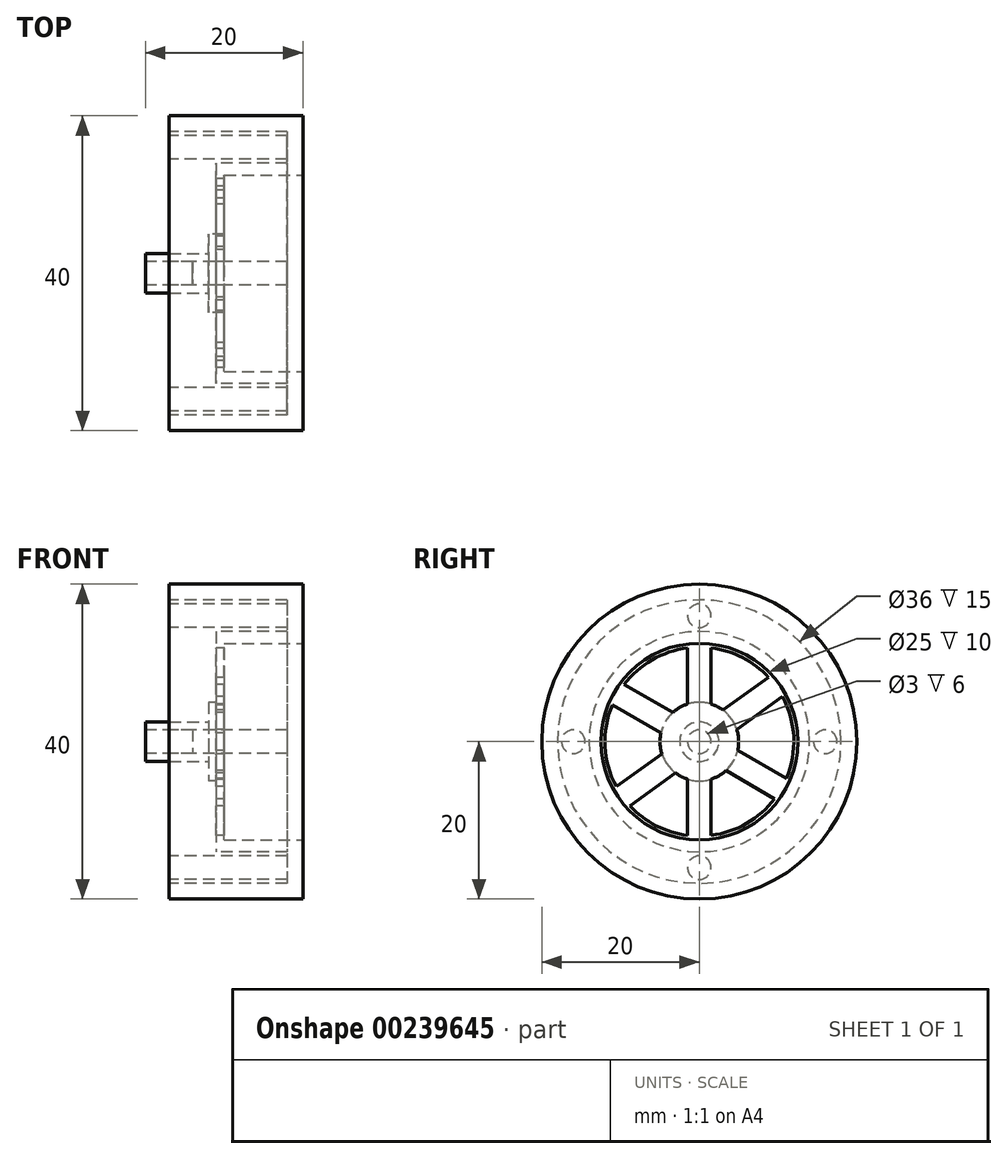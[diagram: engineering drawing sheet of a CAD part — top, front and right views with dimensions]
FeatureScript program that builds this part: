
annotation { "Feature Type Name" : "Feature", "Feature Type Description" : "" }
export const myFeature = defineFeature(function(context is Context, id is Id, definition is map)
    precondition{}
    {
        {
            var Q0;
            Q0=qCreatedBy(makeId("Right.planeOp"),FACE);
            var sketch = newSketch(context, id + "F0", { "sketchPlane" : qUnion([Q0])});
            skCircle(sketch, "E0", {"center": v(0, 0) * mm, "radius": 20 * mm});
            skSolve(sketch);
        }
        {
            var Q0;
            Q0=makeQuery(id+"F0.imprint","IMPRINT",FACE,{"disambiguationData":[TD([[makeQuery(id+"F0.imprint","IMPRINT",EDGE,{"derivedFrom":sQuery(id+"F0.wireOp",EDGE,"E0")}),1.0]])]});
            extrude(context, id + "F1", {"entities" : qUnion([Q0]), "depth" : 17 * mm});
        }
        {
            var Q0;
            Q0=makeQuery(id+"F1.opExtrude","CAP_FACE",FACE,{"disambiguationData":[OSD([sQuery(id+"F0.wireOp",EDGE,"E0")])],"isStart":true});
            var sketch = newSketch(context, id + "F2", { "sketchPlane" : qUnion([Q0])});
            skCircle(sketch, "E1", {"center": v(0, 0) * mm, "radius": 14 * mm});
            skCircle(sketch, "E2", {"center": v(0, 0) * mm, "radius": 18 * mm});
            skLineSegment(sketch, "E3", {"start": v(-17.5, 0) * mm, "end": v(-14.5, 0) * mm});
            skLineSegment(sketch, "E4", {"start": v(0, -14.5) * mm, "end": v(0, -17.5) * mm});
            skLineSegment(sketch, "E5", {"start": v(14.5, 0) * mm, "end": v(17.5, 0) * mm});
            skLineSegment(sketch, "E6", {"start": v(0, 17.5) * mm, "end": v(0, 14.5) * mm});
            skPoint(sketch, "E7", {"position": v(0, 16) * mm});
            skPoint(sketch, "E8", {"position": v(-16, 0) * mm});
            skPoint(sketch, "E9", {"position": v(0, -16) * mm});
            skPoint(sketch, "E10", {"position": v(16, 0) * mm});
            skCircle(sketch, "E11", {"center": v(0, 16) * mm, "radius": 1.5 * mm});
            skCircle(sketch, "E12", {"center": v(-16, 0) * mm, "radius": 1.5 * mm});
            skCircle(sketch, "E13", {"center": v(0, -16) * mm, "radius": 1.5 * mm});
            skCircle(sketch, "E14", {"center": v(16, 0) * mm, "radius": 1.5 * mm});
            skPoint(sketch, "E15.orphan", {"position": v(-18, 0) * mm});
            skPoint(sketch, "E16.orphan", {"position": v(-14, 0) * mm});
            skPoint(sketch, "E17.orphan", {"position": v(0, 14) * mm});
            skPoint(sketch, "E18.orphan", {"position": v(0, 18) * mm});
            skPoint(sketch, "E19.orphan", {"position": v(14, 0) * mm});
            skPoint(sketch, "E20.orphan", {"position": v(18, 0) * mm});
            skPoint(sketch, "E21.orphan", {"position": v(0, -14) * mm});
            skPoint(sketch, "E22.orphan", {"position": v(0, -18) * mm});
            skSolve(sketch);
        }
        {
            var Q0;
            Q0=makeQuery(id+"F2.imprint","IMPRINT",FACE,{"disambiguationData":[TD([[makeQuery(id+"F2.imprint","IMPRINT",EDGE,{"derivedFrom":sQuery(id+"F2.wireOp",EDGE,"E1")}),-1.0]])]});
            extrude(context, id + "F3", {"entities" : qUnion([Q0]), "operationType" : NewBodyOperationType.REMOVE, "oppositeDirection" : true, "depth" : 15 * mm});
        }
        {
            var Q0;
            Q0=makeQuery(id+"F3.boolean.opBoolean","SPLIT",FACE,{"disambiguationData":[TD([makeQuery(id+"F3.opExtrude","SWEPT_FACE",FACE,{"disambiguationData":[OSD([sQuery(id+"F2.wireOp",EDGE,"E1")])]})])],"derivedFrom":makeQuery(id+"F1.opExtrude","CAP_FACE",FACE,{"disambiguationData":[OSD([sQuery(id+"F0.wireOp",EDGE,"E0")])],"isStart":true})});
            extrude(context, id + "F4", {"entities" : qUnion([Q0]), "operationType" : NewBodyOperationType.REMOVE, "oppositeDirection" : true, "depth" : 6 * mm});
        }
        {
            var Q0;
            Q0=makeQuery(id+"F4.boolean.opBoolean","COPY",FACE,{"derivedFrom":makeQuery(id+"F4.opExtrude","CAP_FACE",FACE,{"disambiguationData":[OSD([sQuery(id+"F0.wireOp",EDGE,"E0")])],"isStart":false})});
            var sketch = newSketch(context, id + "F5", { "sketchPlane" : qUnion([Q0])});
            skCircle(sketch, "E23", {"center": v(0, 0) * mm, "radius": 5 * mm});
            skCircle(sketch, "E24", {"center": v(0, 0) * mm, "radius": 12 * mm});
            skLineSegment(sketch, "E25", {"start": v(0, 12) * mm, "end": v(0, -12) * mm});
            skLineSegment(sketch, "E26", {"start": v(-10.4, -6) * mm, "end": v(10.4, 6) * mm});
            skLineSegment(sketch, "E27", {"start": v(9.75, -7) * mm, "end": v(-9.75, 7) * mm});
            skLineSegment(sketch, "E28.left", {"start": v(-1.5, 11.9) * mm, "end": v(-1.5, 4.77) * mm});
            skLineSegment(sketch, "E28.right", {"start": v(1.5, 11.9) * mm, "end": v(1.5, 4.77) * mm});
            skLineSegment(sketch, "E29", {"start": v(-1.5, 8.34) * mm, "end": v(0, 8.34) * mm, "construction": true});
            skLineSegment(sketch, "E30", {"start": v(1.5, 8.34) * mm, "end": v(0, 8.34) * mm, "construction": true});
            skPoint(sketch, "E31.orphan", {"position": v(-1.5, 4.28) * mm});
            skPoint(sketch, "E32.orphan", {"position": v(1.5, 4.28) * mm});
            skPoint(sketch, "E33.orphan", {"position": v(-1.5, 12.4) * mm});
            skPoint(sketch, "E34.orphan", {"position": v(1.5, 12.4) * mm});
            skLineSegment(sketch, "E35", {"start": v(4.88, 1.09) * mm, "end": v(11.06, 4.65) * mm});
            skLineSegment(sketch, "E36", {"start": v(3.38, 3.68) * mm, "end": v(9.56, 7.25) * mm});
            skLineSegment(sketch, "E37", {"start": v(7.01, 5.78) * mm, "end": v(7.76, 4.48) * mm, "construction": true});
            skLineSegment(sketch, "E38", {"start": v(7.76, 4.48) * mm, "end": v(8.51, 3.18) * mm, "construction": true});
            skLineSegment(sketch, "E39", {"start": v(4.75, -1.56) * mm, "end": v(10.55, -5.72) * mm});
            skLineSegment(sketch, "E40", {"start": v(3, -4) * mm, "end": v(8.8, -8.16) * mm});
            skLineSegment(sketch, "E41", {"start": v(8.03, -3.91) * mm, "end": v(7.16, -5.13) * mm, "construction": true});
            skLineSegment(sketch, "E42", {"start": v(7.16, -5.13) * mm, "end": v(6.28, -6.35) * mm, "construction": true});
            skLineSegment(sketch, "E43", {"start": v(-1.5, -4.77) * mm, "end": v(-1.5, -11.9) * mm});
            skLineSegment(sketch, "E44", {"start": v(1.5, -4.77) * mm, "end": v(1.5, -11.9) * mm});
            skLineSegment(sketch, "E45", {"start": v(-1.5, -8.34) * mm, "end": v(0, -8.34) * mm, "construction": true});
            skLineSegment(sketch, "E46", {"start": v(0, -8.34) * mm, "end": v(1.5, -8.34) * mm, "construction": true});
            skPoint(sketch, "E46.endSnap0", {"position": v(1.5, -8.34) * mm});
            skLineSegment(sketch, "E47", {"start": v(-3.38, -3.68) * mm, "end": v(-9.56, -7.25) * mm});
            skLineSegment(sketch, "E48", {"start": v(-4.88, -1.09) * mm, "end": v(-11.06, -4.65) * mm});
            skPoint(sketch, "E49.endSnap0", {"position": v(-6.47, -5.47) * mm});
            skLineSegment(sketch, "E50", {"start": v(-6.93, -4) * mm, "end": v(-6.18, -5.3) * mm, "construction": true});
            skLineSegment(sketch, "E51", {"start": v(-6.93, -4) * mm, "end": v(-7.68, -2.7) * mm, "construction": true});
            skLineSegment(sketch, "E52", {"start": v(-8.8, 8.16) * mm, "end": v(-3, 4) * mm});
            skLineSegment(sketch, "E53", {"start": v(-10.55, 5.72) * mm, "end": v(-4.75, 1.56) * mm});
            skLineSegment(sketch, "E54", {"start": v(-7.15, 5.12) * mm, "end": v(-6.27, 6.34) * mm, "construction": true});
            skLineSegment(sketch, "E55", {"start": v(-7.15, 5.12) * mm, "end": v(-8.02, 3.9) * mm, "construction": true});
            skSolve(sketch);
        }
        {
            var Q0;
            {var subQ0=sQuery(id+"F5.wireOp",EDGE,"E48");Q0=makeQuery(id+"F5.imprint","IMPRINT",FACE,{"disambiguationData":[TD([[makeQuery(id+"F5.imprint","IMPRINT",EDGE,{"derivedFrom":subQ0}),-1.0]])]});}
            var Q1;
            {var subQ0=sQuery(id+"F5.wireOp",EDGE,"E28.left");Q1=makeQuery(id+"F5.imprint","IMPRINT",FACE,{"disambiguationData":[TD([[makeQuery(id+"F5.imprint","IMPRINT",EDGE,{"derivedFrom":subQ0}),-1.0]])]});}
            var Q2;
            {var subQ0=sQuery(id+"F5.wireOp",EDGE,"E28.right");Q2=makeQuery(id+"F5.imprint","IMPRINT",FACE,{"disambiguationData":[TD([[makeQuery(id+"F5.imprint","IMPRINT",EDGE,{"derivedFrom":subQ0}),1.0]])]});}
            var Q3;
            {var subQ0=sQuery(id+"F5.wireOp",EDGE,"E35");Q3=makeQuery(id+"F5.imprint","IMPRINT",FACE,{"disambiguationData":[TD([[makeQuery(id+"F5.imprint","IMPRINT",EDGE,{"derivedFrom":subQ0}),-1.0]])]});}
            var Q4;
            {var subQ0=sQuery(id+"F5.wireOp",EDGE,"E40");Q4=makeQuery(id+"F5.imprint","IMPRINT",FACE,{"disambiguationData":[TD([[makeQuery(id+"F5.imprint","IMPRINT",EDGE,{"derivedFrom":subQ0}),-1.0]])]});}
            var Q5;
            {var subQ0=sQuery(id+"F5.wireOp",EDGE,"E43");Q5=makeQuery(id+"F5.imprint","IMPRINT",FACE,{"disambiguationData":[TD([[makeQuery(id+"F5.imprint","IMPRINT",EDGE,{"derivedFrom":subQ0}),-1.0]])]});}
            extrude(context, id + "F6", {"entities" : qUnion([Q0, Q1, Q2, Q3, Q4, Q5]), "operationType" : NewBodyOperationType.REMOVE, "oppositeDirection" : true, "depth" : 25 * mm});
        }
        {
            var Q0;
            Q0=makeQuery(id+"F1.opExtrude","CAP_FACE",FACE,{"disambiguationData":[OSD([sQuery(id+"F0.wireOp",EDGE,"E0")])],"isStart":false});
            var sketch = newSketch(context, id + "F7", { "sketchPlane" : qUnion([Q0])});
            skCircle(sketch, "E56", {"center": v(0, 0) * mm, "radius": 12.5 * mm});
            skSolve(sketch);
        }
        {
            var Q0;
            Q0 = qSketchRegion(id + "F7", true);
            extrude(context, id + "F8", {"entities" : qUnion([Q0]), "operationType" : NewBodyOperationType.REMOVE, "oppositeDirection" : true, "depth" : 10 * mm});
        }
        {
            var Q0;
            Q0=makeQuery(id+"F4.boolean.opBoolean","COPY",FACE,{"derivedFrom":makeQuery(id+"F4.opExtrude","CAP_FACE",FACE,{"disambiguationData":[OSD([sQuery(id+"F0.wireOp",EDGE,"E0")])],"isStart":false})});
            var sketch = newSketch(context, id + "F9", { "sketchPlane" : qUnion([Q0])});
            skCircle(sketch, "E57", {"center": v(0, 0) * mm, "radius": 5 * mm});
            skSolve(sketch);
        }
        {
            var Q0;
            Q0 = qSketchRegion(id + "F9", true);
            extrude(context, id + "F10", {"entities" : qUnion([Q0]), "operationType" : NewBodyOperationType.ADD, "depth" : 1 * mm});
        }
        {
            var Q0;
            Q0=makeQuery(id+"F10.opExtrude","CAP_FACE",FACE,{"disambiguationData":[OSD([sQuery(id+"F9.wireOp",EDGE,"E57")])],"isStart":false});
            var sketch = newSketch(context, id + "F11", { "sketchPlane" : qUnion([Q0])});
            skCircle(sketch, "E58", {"center": v(0, 0) * mm, "radius": 2.5 * mm});
            skSolve(sketch);
        }
        {
            var Q0;
            Q0 = qSketchRegion(id + "F11", true);
            extrude(context, id + "F12", {"entities" : qUnion([Q0]), "operationType" : NewBodyOperationType.ADD, "depth" : 8 * mm});
        }
        {
            var Q0;
            Q0=makeQuery(id+"F12.opExtrude","CAP_FACE",FACE,{"disambiguationData":[OSD([sQuery(id+"F11.wireOp",EDGE,"E58")])],"isStart":false});
            var sketch = newSketch(context, id + "F13", { "sketchPlane" : qUnion([Q0])});
            skCircle(sketch, "E59", {"center": v(0, 0) * mm, "radius": 1.5 * mm});
            skSolve(sketch);
        }
        {
            var Q0;
            Q0 = qSketchRegion(id + "F13", true);
            extrude(context, id + "F14", {"entities" : qUnion([Q0]), "operationType" : NewBodyOperationType.REMOVE, "oppositeDirection" : true, "depth" : 6 * mm});
        }
    });
